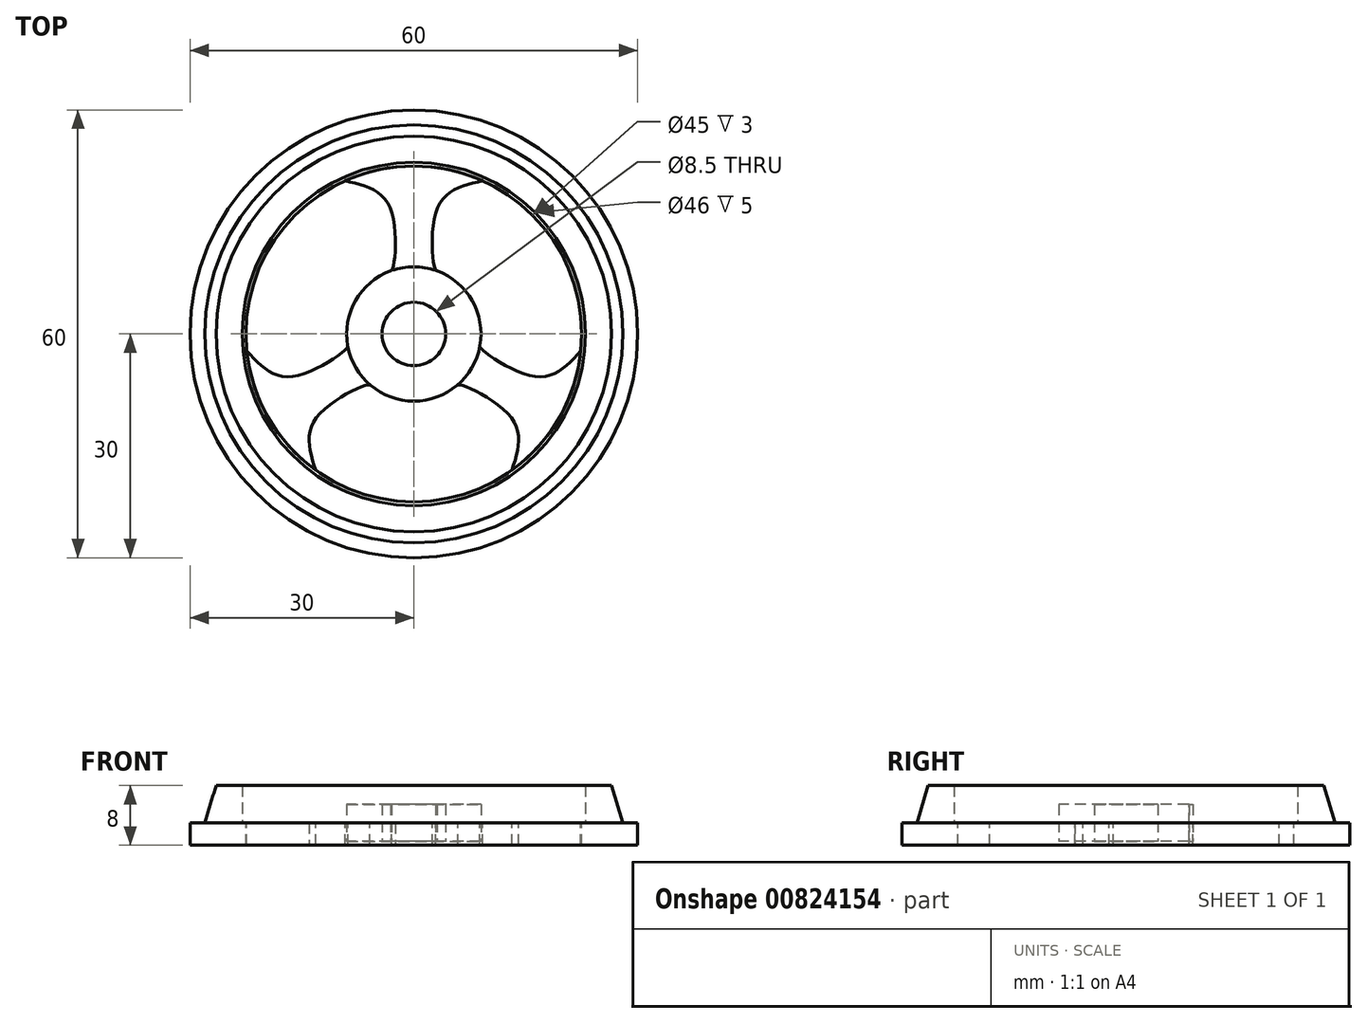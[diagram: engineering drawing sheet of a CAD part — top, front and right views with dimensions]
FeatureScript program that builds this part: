
annotation { "Feature Type Name" : "Feature", "Feature Type Description" : "" }
export const myFeature = defineFeature(function(context is Context, id is Id, definition is map)
    precondition{}
    {
        {
            var Q0;
            Q0=qCreatedBy(makeId("Top.planeOp"),FACE);
            var sketch = newSketch(context, id + "F0", { "sketchPlane" : qUnion([Q0])});
            skCircle(sketch, "E0", {"center": v(0, 0) * mm, "radius": 26.5 * mm});
            skCircle(sketch, "E1", {"center": v(0, 0) * mm, "radius": 30 * mm});
            skCircle(sketch, "E2", {"center": v(0, 0) * mm, "radius": 4.25 * mm});
            skCircle(sketch, "E3", {"center": v(0, 0) * mm, "radius": 9 * mm});
            skCircle(sketch, "E4", {"center": v(0, 0) * mm, "radius": 22.5 * mm});
            skLineSegment(sketch, "E5", {"start": v(-30, 0) * mm, "end": v(-22.5, 0) * mm, "construction": true});
            skArc(sketch, "E6", {"start": v(0, -15) * mm, "mid": v(-0.33, -11.89) * mm, "end": v(-1.3, -8.9) * mm});
            skPoint(sketch, "E6.first.point", {"position": v(-28.67, -8.83) * mm});
            skPoint(sketch, "E6.second.point", {"position": v(-15, 0) * mm});
            skPoint(sketch, "E6.third.point", {"position": v(0, -15) * mm});
            skLineSegment(sketch, "E7.trimOffspring", {"start": v(-15, 0) * mm, "end": v(0, 0) * mm, "construction": true});
            skLineSegment(sketch, "E8", {"start": v(0, 0) * mm, "end": v(-3.05, -2.96) * mm, "construction": true});
            skLineSegment(sketch, "E9.trimOffspring", {"start": v(-16.17, -15.65) * mm, "end": v(-16.94, -16.4) * mm, "construction": true});
            skFitSpline(sketch, "E10", {"points": [v(-9.22, 20.52) * mm, v(-3.2, 16.94) * mm, v(-2.95, 8.5) * mm, v(-3.12, 8.44) * mm], "startDerivative": vector(16.81, -3.73) * mm, "endDerivative": vector(-1.62, -0.22) * mm});
            skFitSpline(sketch, "E11.MirrorCS", {"points": [v(9.22, 20.52) * mm, v(3.2, 16.94) * mm, v(2.95, 8.5) * mm, v(3.12, 8.44) * mm], "startDerivative": vector(-16.81, -3.73) * mm, "endDerivative": vector(1.62, -0.22) * mm});
            skSolve(sketch);
        }
        {
            var Q0;
            Q0=qCreatedBy(makeId("Front.planeOp"),FACE);
            var sketch = newSketch(context, id + "F1", { "sketchPlane" : qUnion([Q0])});
            skLineSegment(sketch, "E12", {"start": v(-28, 0) * mm, "end": v(-26.5, 5) * mm});
            skLineSegment(sketch, "E13", {"start": v(-23, 5) * mm, "end": v(-23, 0) * mm});
            skLineSegment(sketch, "E14", {"start": v(-28, 0) * mm, "end": v(-23, 0) * mm});
            skLineSegment(sketch, "E15", {"start": v(0, 0) * mm, "end": v(0, 30.56) * mm, "construction": true});
            skLineSegment(sketch, "E16", {"start": v(-23, 5) * mm, "end": v(-26.5, 5) * mm});
            skPoint(sketch, "E17.orphan", {"position": v(-25, 10) * mm});
            skLineSegment(sketch, "E18", {"start": v(-28, 0) * mm, "end": v(0, 0) * mm, "construction": true});
            skSolve(sketch);
        }
        {
            var Q0;
            Q0=makeQuery(id+"F1.imprint","IMPRINT",FACE,{"disambiguationData":[TD([[makeQuery(id+"F1.imprint","IMPRINT",EDGE,{"derivedFrom":sQuery(id+"F1.wireOp",EDGE,"E12")}),-1.0]])]});
            var Q1;
            Q1=sQuery(id+"F1.wireOp",EDGE,"E15");
            revolve(context, id + "F2", {"surfaceOperationType" : NewSurfaceOperationType.NEW, "entities" : qUnion([Q0]), "axis" : qUnion([Q1]), "revolveType" : RevolveType.FULL});
        }
        {
            var Q0;
            Q0=makeQuery(id+"F0.imprint","IMPRINT",FACE,{"disambiguationData":[TD([[makeQuery(id+"F0.imprint","IMPRINT",EDGE,{"derivedFrom":sQuery(id+"F0.wireOp",EDGE,"E2")}),-1.0]])]});
            extrude(context, id + "F3", {"entities" : qUnion([Q0]), "depth" : 5 * mm, "offsetDistance" : 25 * mm, "symmetric" : true});
        }
        {
            var Q0;
            {var subQ0=sQuery(id+"F0.wireOp",EDGE,"E11.MirrorCS");var subQ1=sQuery(id+"F0.wireOp",EDGE,"E3");var subQ2=makeQuery(id+"F0.imprint","INTERSECT",VERTEX,{"disambiguationData":[OD(1.0)],"derivedFrom":[subQ1,subQ0]});Q0=makeQuery(id+"F0.imprint","IMPRINT",FACE,{"disambiguationData":[TD([[makeQuery(id+"F0.imprint","IMPRINT",EDGE,{"disambiguationData":[TD([[subQ2,-1.0]])],"derivedFrom":subQ1}),-1.0]])]});}
            extrude(context, id + "F4", {"entities" : qUnion([Q0]), "oppositeDirection" : true, "depth" : 3 * mm, "offsetDistance" : 25 * mm});
        }
        {
            var Q0;
            Q0=makeQuery(id+"F0.imprint","IMPRINT",FACE,{"disambiguationData":[TD([[makeQuery(id+"F0.imprint","IMPRINT",EDGE,{"derivedFrom":sQuery(id+"F0.wireOp",EDGE,"E0")}),-1.0]])]});
            var Q1;
            Q1=makeQuery(id+"F0.imprint","IMPRINT",FACE,{"disambiguationData":[TD([[makeQuery(id+"F0.imprint","IMPRINT",EDGE,{"derivedFrom":sQuery(id+"F0.wireOp",EDGE,"E0")}),1.0]])]});
            extrude(context, id + "F5", {"entities" : qUnion([Q0, Q1]), "oppositeDirection" : true, "depth" : 3 * mm, "offsetDistance" : 25 * mm});
        }
        {
            var Q0;
            Q0=makeQuery(id+"F4.opExtrude","SWEPT_BODY",BODY,{"disambiguationData":[OSD([sQuery(id+"F0.wireOp",EDGE,"E3"),sQuery(id+"F0.wireOp",EDGE,"E4"),sQuery(id+"F0.wireOp",EDGE,"E10"),sQuery(id+"F0.wireOp",EDGE,"E11.MirrorCS")])]});
            var Q1;
            Q1=sQuery(id+"F1.wireOp",EDGE,"E15");
            circularPattern(context, id + "F6", {"entities" : qUnion([Q0]), "axis" : qUnion([Q1]), "angle" : 360 * degree, "instanceCount" : 3, "equalSpace" : true});
        }
    });
